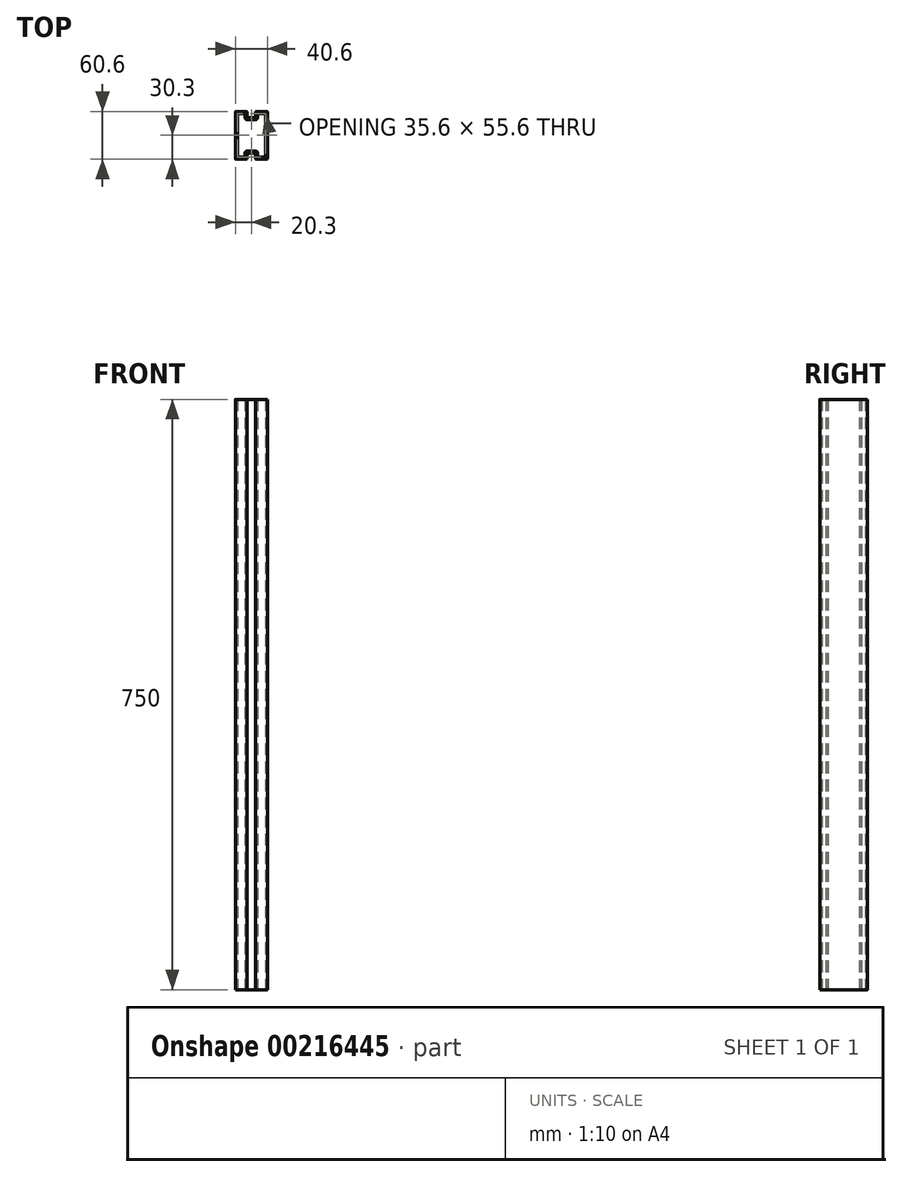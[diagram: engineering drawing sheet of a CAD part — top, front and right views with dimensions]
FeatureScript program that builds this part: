
annotation { "Feature Type Name" : "Feature", "Feature Type Description" : "" }
export const myFeature = defineFeature(function(context is Context, id is Id, definition is map)
    precondition{}
    {
        {
            var Q0;
            Q0=qCreatedBy(makeId("Top.planeOp"),FACE);
            var sketch = newSketch(context, id + "F0", { "sketchPlane" : qUnion([Q0])});
            skLineSegment(sketch, "E0.bottom", {"start": v(-21.9, -32.5) * mm, "end": v(21.9, -32.5) * mm});
            skLineSegment(sketch, "E0.top", {"start": v(-21.9, 32.5) * mm, "end": v(21.9, 32.5) * mm});
            skLineSegment(sketch, "E0.left", {"start": v(-22.5, -31.9) * mm, "end": v(-22.5, 31.9) * mm});
            skLineSegment(sketch, "E0.right", {"start": v(22.5, -31.9) * mm, "end": v(22.5, 31.9) * mm});
            skPoint(sketch, "E1.visualSharp", {"position": v(-22.5, 32.5) * mm});
            skArc(sketch, "E1.filletArc", {"start": v(-21.9, 32.5) * mm, "mid": v(-22.32, 32.32) * mm, "end": v(-22.5, 31.9) * mm});
            skPoint(sketch, "E2.visualSharp", {"position": v(22.5, 32.5) * mm});
            skArc(sketch, "E2.filletArc", {"start": v(22.5, 31.9) * mm, "mid": v(22.32, 32.32) * mm, "end": v(21.9, 32.5) * mm});
            skPoint(sketch, "E3.visualSharp", {"position": v(-22.5, -32.5) * mm});
            skArc(sketch, "E3.filletArc", {"start": v(-22.5, -31.9) * mm, "mid": v(-22.32, -32.32) * mm, "end": v(-21.9, -32.5) * mm});
            skPoint(sketch, "E4.visualSharp", {"position": v(22.5, -32.5) * mm});
            skArc(sketch, "E4.filletArc", {"start": v(21.9, -32.5) * mm, "mid": v(22.32, -32.32) * mm, "end": v(22.5, -31.9) * mm});
            skLineSegment(sketch, "E5.0", {"start": v(-20.5, -30) * mm, "end": v(-20.5, 30) * mm});
            skLineSegment(sketch, "E5.2", {"start": v(20.5, -30) * mm, "end": v(20.5, 30) * mm});
            skLineSegment(sketch, "E5.3", {"start": v(-20, 30.5) * mm, "end": v(-5.5, 30.5) * mm});
            skPoint(sketch, "E6.visualSharp", {"position": v(-20.5, 30.5) * mm});
            skArc(sketch, "E6.filletArc", {"start": v(-20, 30.5) * mm, "mid": v(-20.35, 30.35) * mm, "end": v(-20.5, 30) * mm});
            skPoint(sketch, "E7.visualSharp", {"position": v(20.5, 30.5) * mm});
            skArc(sketch, "E7.filletArc", {"start": v(20.5, 30) * mm, "mid": v(20.35, 30.35) * mm, "end": v(20, 30.5) * mm});
            skPoint(sketch, "E8.visualSharp", {"position": v(-20.5, -30.5) * mm});
            skArc(sketch, "E8.filletArc", {"start": v(-20.5, -30) * mm, "mid": v(-20.35, -30.35) * mm, "end": v(-20, -30.5) * mm});
            skPoint(sketch, "E9.visualSharp", {"position": v(20.5, -30.5) * mm});
            skArc(sketch, "E9.filletArc", {"start": v(20, -30.5) * mm, "mid": v(20.35, -30.35) * mm, "end": v(20.5, -30) * mm});
            skLineSegment(sketch, "E10", {"start": v(0, 32.5) * mm, "end": v(0, -32.5) * mm, "construction": true});
            skLineSegment(sketch, "E11", {"start": v(22.5, 0) * mm, "end": v(-22.5, 0) * mm, "construction": true});
            skArc(sketch, "E12", {"start": v(-5, 28) * mm, "mid": v(-4.25, 25.36) * mm, "end": v(-2.22, 23.52) * mm});
            skLineSegment(sketch, "E13", {"start": v(-5, 28) * mm, "end": v(-5, 30) * mm});
            skLineSegment(sketch, "E14", {"start": v(5, 28) * mm, "end": v(5, 30) * mm});
            skArc(sketch, "E15", {"start": v(1.68, 26.01) * mm, "mid": v(0, 30.6) * mm, "end": v(-1.68, 26.01) * mm});
            skLineSegment(sketch, "E16", {"start": v(-1.5, 25.63) * mm, "end": v(-1.5, 23.97) * mm});
            skLineSegment(sketch, "E17.MirrorCS", {"start": v(1.5, 25.63) * mm, "end": v(1.5, 23.97) * mm});
            skLineSegment(sketch, "E18.trimOffspring", {"start": v(5.5, 30.5) * mm, "end": v(20, 30.5) * mm});
            skArc(sketch, "E19.trimOffspring", {"start": v(2.22, 23.52) * mm, "mid": v(4.25, 25.36) * mm, "end": v(5, 28) * mm});
            skPoint(sketch, "E20.visualSharp", {"position": v(-5, 30.5) * mm});
            skArc(sketch, "E20.filletArc", {"start": v(-5, 30) * mm, "mid": v(-5.15, 30.35) * mm, "end": v(-5.5, 30.5) * mm});
            skPoint(sketch, "E21.visualSharp", {"position": v(5, 30.5) * mm});
            skArc(sketch, "E21.filletArc", {"start": v(5.5, 30.5) * mm, "mid": v(5.15, 30.35) * mm, "end": v(5, 30) * mm});
            skPoint(sketch, "E22.visualSharp", {"position": v(1.5, 23.23) * mm});
            skArc(sketch, "E22.filletArc", {"start": v(1.5, 23.97) * mm, "mid": v(1.74, 23.54) * mm, "end": v(2.22, 23.52) * mm});
            skPoint(sketch, "E23.visualSharp", {"position": v(-1.5, 23.23) * mm});
            skArc(sketch, "E23.filletArc", {"start": v(-2.22, 23.52) * mm, "mid": v(-1.74, 23.54) * mm, "end": v(-1.5, 23.97) * mm});
            skPoint(sketch, "E24.visualSharp", {"position": v(-1.5, 25.88) * mm});
            skArc(sketch, "E24.filletArc", {"start": v(-1.5, 25.63) * mm, "mid": v(-1.55, 25.84) * mm, "end": v(-1.68, 26.01) * mm});
            skPoint(sketch, "E25.visualSharp", {"position": v(1.5, 25.88) * mm});
            skArc(sketch, "E25.filletArc", {"start": v(1.68, 26.01) * mm, "mid": v(1.55, 25.84) * mm, "end": v(1.5, 25.63) * mm});
            skArc(sketch, "E26.MirrorCS", {"start": v(-1.5, -25.63) * mm, "mid": v(-1.55, -25.84) * mm, "end": v(-1.68, -26.01) * mm});
            skArc(sketch, "E27.MirrorCS", {"start": v(1.68, -26.01) * mm, "mid": v(1.55, -25.84) * mm, "end": v(1.5, -25.63) * mm});
            skArc(sketch, "E28.MirrorCS", {"start": v(-2.22, -23.52) * mm, "mid": v(-1.74, -23.54) * mm, "end": v(-1.5, -23.97) * mm});
            skArc(sketch, "E29.MirrorCS", {"start": v(5.5, -30.5) * mm, "mid": v(5.15, -30.35) * mm, "end": v(5, -30) * mm});
            skLineSegment(sketch, "E30.MirrorCS", {"start": v(-1.5, -25.63) * mm, "end": v(-1.5, -23.97) * mm});
            skLineSegment(sketch, "E31.MirrorCS", {"start": v(1.5, -25.63) * mm, "end": v(1.5, -23.97) * mm});
            skArc(sketch, "E32.MirrorCS", {"start": v(-5, -30) * mm, "mid": v(-5.15, -30.35) * mm, "end": v(-5.5, -30.5) * mm});
            skArc(sketch, "E33.MirrorCS", {"start": v(1.5, -23.97) * mm, "mid": v(1.74, -23.54) * mm, "end": v(2.22, -23.52) * mm});
            skPoint(sketch, "E34.MirrorP", {"position": v(1.5, -25.88) * mm});
            skLineSegment(sketch, "E35.MirrorCS", {"start": v(-20, -30.5) * mm, "end": v(-5.5, -30.5) * mm});
            skArc(sketch, "E36.MirrorCS", {"start": v(2.22, -23.52) * mm, "mid": v(4.25, -25.36) * mm, "end": v(5, -28) * mm});
            skPoint(sketch, "E37.MirrorP", {"position": v(-1.5, -23.23) * mm});
            skArc(sketch, "E38.MirrorCS", {"start": v(-5, -28) * mm, "mid": v(-4.25, -25.36) * mm, "end": v(-2.22, -23.52) * mm});
            skPoint(sketch, "E39.MirrorP", {"position": v(1.5, -23.23) * mm});
            skArc(sketch, "E40.MirrorCS", {"start": v(1.68, -26.01) * mm, "mid": v(0, -30.6) * mm, "end": v(-1.68, -26.01) * mm});
            skLineSegment(sketch, "E41.MirrorCS", {"start": v(5, -28) * mm, "end": v(5, -30) * mm});
            skLineSegment(sketch, "E42.MirrorCS", {"start": v(0, -32.5) * mm, "end": v(0, 32.5) * mm, "construction": true});
            skLineSegment(sketch, "E43.MirrorCS", {"start": v(-5, -28) * mm, "end": v(-5, -30) * mm});
            skPoint(sketch, "E44.MirrorP", {"position": v(-5, -30.5) * mm});
            skPoint(sketch, "E45.MirrorP", {"position": v(5, -30.5) * mm});
            skLineSegment(sketch, "E46.MirrorCS", {"start": v(5.5, -30.5) * mm, "end": v(20, -30.5) * mm});
            skPoint(sketch, "E47.MirrorP", {"position": v(-1.5, -25.88) * mm});
            skSolve(sketch);
        }
        {
            var Q0;
            Q0=makeQuery(id+"F0.imprint","IMPRINT",FACE,{"disambiguationData":[TD([[makeQuery(id+"F0.imprint","IMPRINT",EDGE,{"derivedFrom":sQuery(id+"F0.wireOp",EDGE,"E5.0")}),-1.0]])]});
            var sketch = newSketch(context, id + "F1", { "sketchPlane" : qUnion([Q0])});
            skLineSegment(sketch, "E48.0", {"start": v(20.3, -29.8) * mm, "end": v(20.3, 29.8) * mm});
            skLineSegment(sketch, "E49.0", {"start": v(-20.3, -29.8) * mm, "end": v(-20.3, 29.8) * mm});
            skLineSegment(sketch, "E50.0", {"start": v(-19.8, 30.3) * mm, "end": v(-6, 30.3) * mm});
            skLineSegment(sketch, "E51.0", {"start": v(6, 30.3) * mm, "end": v(19.8, 30.3) * mm});
            skPoint(sketch, "E52.visualSharp", {"position": v(-20.3, 30.3) * mm});
            skArc(sketch, "E52.filletArc", {"start": v(-19.8, 30.3) * mm, "mid": v(-20.15, 30.15) * mm, "end": v(-20.3, 29.8) * mm});
            skPoint(sketch, "E53.visualSharp", {"position": v(20.3, 30.3) * mm});
            skArc(sketch, "E53.filletArc", {"start": v(20.3, 29.8) * mm, "mid": v(20.15, 30.15) * mm, "end": v(19.8, 30.3) * mm});
            skPoint(sketch, "E54.visualSharp", {"position": v(-20.3, -30.3) * mm});
            skArc(sketch, "E54.filletArc", {"start": v(-20.3, -29.8) * mm, "mid": v(-20.15, -30.15) * mm, "end": v(-19.8, -30.3) * mm});
            skPoint(sketch, "E55.visualSharp", {"position": v(20.3, -30.3) * mm});
            skArc(sketch, "E55.filletArc", {"start": v(19.8, -30.3) * mm, "mid": v(20.15, -30.15) * mm, "end": v(20.3, -29.8) * mm});
            skLineSegment(sketch, "E56", {"start": v(-5.5, 29.8) * mm, "end": v(-5.5, 22.8) * mm});
            skLineSegment(sketch, "E57", {"start": v(-5, 22.3) * mm, "end": v(5, 22.3) * mm});
            skLineSegment(sketch, "E58", {"start": v(5.5, 22.8) * mm, "end": v(5.5, 29.8) * mm});
            skPoint(sketch, "E59.visualSharp", {"position": v(-5.5, 22.3) * mm});
            skArc(sketch, "E59.filletArc", {"start": v(-5.5, 22.8) * mm, "mid": v(-5.35, 22.45) * mm, "end": v(-5, 22.3) * mm});
            skPoint(sketch, "E60.visualSharp", {"position": v(-5.5, 30.3) * mm});
            skArc(sketch, "E60.filletArc", {"start": v(-5.5, 29.8) * mm, "mid": v(-5.65, 30.15) * mm, "end": v(-6, 30.3) * mm});
            skPoint(sketch, "E61.visualSharp", {"position": v(5.5, 30.3) * mm});
            skArc(sketch, "E61.filletArc", {"start": v(6, 30.3) * mm, "mid": v(5.65, 30.15) * mm, "end": v(5.5, 29.8) * mm});
            skPoint(sketch, "E62.visualSharp", {"position": v(5.5, 22.3) * mm});
            skArc(sketch, "E62.filletArc", {"start": v(5, 22.3) * mm, "mid": v(5.35, 22.45) * mm, "end": v(5.5, 22.8) * mm});
            skLineSegment(sketch, "E63", {"start": v(-20.3, 0) * mm, "end": v(20.3, 0) * mm, "construction": true});
            skLineSegment(sketch, "E64.MirrorCS", {"start": v(-5.5, -29.8) * mm, "end": v(-5.5, -22.8) * mm});
            skLineSegment(sketch, "E65.MirrorCS", {"start": v(5.5, -22.8) * mm, "end": v(5.5, -29.8) * mm});
            skArc(sketch, "E66.MirrorCS", {"start": v(-5.5, -22.8) * mm, "mid": v(-5.35, -22.45) * mm, "end": v(-5, -22.3) * mm});
            skArc(sketch, "E67.MirrorCS", {"start": v(5, -22.3) * mm, "mid": v(5.35, -22.45) * mm, "end": v(5.5, -22.8) * mm});
            skPoint(sketch, "E68.MirrorP", {"position": v(5.5, -22.3) * mm});
            skLineSegment(sketch, "E69.MirrorCS", {"start": v(-5, -22.3) * mm, "end": v(5, -22.3) * mm});
            skPoint(sketch, "E70.MirrorP", {"position": v(-5.5, -22.3) * mm});
            skArc(sketch, "E71.MirrorCS", {"start": v(-5.5, -29.8) * mm, "mid": v(-5.65, -30.15) * mm, "end": v(-6, -30.3) * mm});
            skLineSegment(sketch, "E72.MirrorCS", {"start": v(-19.8, -30.3) * mm, "end": v(-6, -30.3) * mm});
            skLineSegment(sketch, "E73.MirrorCS", {"start": v(6, -30.3) * mm, "end": v(19.8, -30.3) * mm});
            skArc(sketch, "E74.MirrorCS", {"start": v(6, -30.3) * mm, "mid": v(5.65, -30.15) * mm, "end": v(5.5, -29.8) * mm});
            skLineSegment(sketch, "E75.0", {"start": v(-5, -19.8) * mm, "end": v(5, -19.8) * mm});
            skArc(sketch, "E76.0", {"start": v(-8, -22.8) * mm, "mid": v(-7.12, -20.68) * mm, "end": v(-5, -19.8) * mm});
            skLineSegment(sketch, "E77.0", {"start": v(-17.8, -27.8) * mm, "end": v(-8, -27.8) * mm});
            skLineSegment(sketch, "E77.1", {"start": v(-17.8, -27.8) * mm, "end": v(-17.8, 27.8) * mm});
            skLineSegment(sketch, "E77.2", {"start": v(-17.8, 27.8) * mm, "end": v(-8, 27.8) * mm});
            skLineSegment(sketch, "E77.3", {"start": v(-8, 27.8) * mm, "end": v(-8, 22.8) * mm});
            skArc(sketch, "E77.4", {"start": v(-8, 22.8) * mm, "mid": v(-7.12, 20.68) * mm, "end": v(-5, 19.8) * mm});
            skLineSegment(sketch, "E77.5", {"start": v(8, -22.8) * mm, "end": v(8, -27.8) * mm});
            skArc(sketch, "E77.6", {"start": v(5, -19.8) * mm, "mid": v(7.12, -20.68) * mm, "end": v(8, -22.8) * mm});
            skLineSegment(sketch, "E77.9", {"start": v(8, -27.8) * mm, "end": v(17.8, -27.8) * mm});
            skLineSegment(sketch, "E77.10", {"start": v(17.8, -27.8) * mm, "end": v(17.8, 27.8) * mm});
            skLineSegment(sketch, "E77.11", {"start": v(8, 27.8) * mm, "end": v(17.8, 27.8) * mm});
            skLineSegment(sketch, "E77.12", {"start": v(8, 22.8) * mm, "end": v(8, 27.8) * mm});
            skArc(sketch, "E77.13", {"start": v(5, 19.8) * mm, "mid": v(7.12, 20.68) * mm, "end": v(8, 22.8) * mm});
            skLineSegment(sketch, "E77.14", {"start": v(-8, -27.8) * mm, "end": v(-8, -22.8) * mm});
            skLineSegment(sketch, "E77.15", {"start": v(-5, 19.8) * mm, "end": v(5, 19.8) * mm});
            skSolve(sketch);
        }
        {
            var Q0;
            Q0 = qSketchRegion(id + "F1", true);
            extrude(context, id + "F2", {"entities" : qUnion([Q0]), "depth" : 750 * mm});
        }
    });
